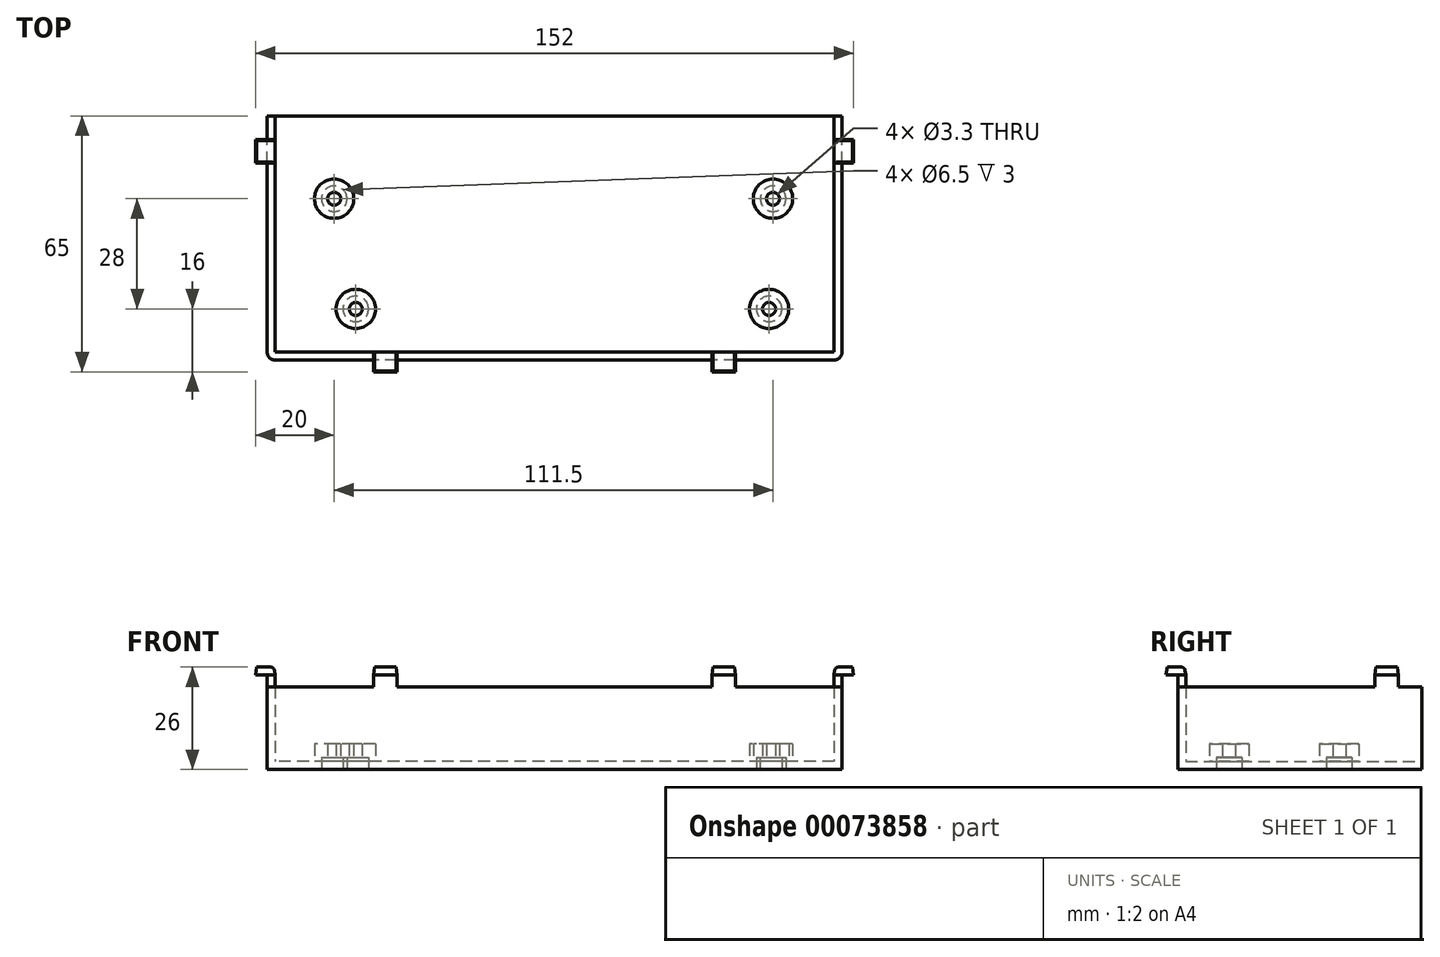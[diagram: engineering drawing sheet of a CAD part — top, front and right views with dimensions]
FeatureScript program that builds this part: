
annotation { "Feature Type Name" : "Feature", "Feature Type Description" : "" }
export const myFeature = defineFeature(function(context is Context, id is Id, definition is map)
    precondition{}
    {
        {
            var Q0;
            Q0=qCreatedBy(makeId("Top.planeOp"),FACE);
            var sketch = newSketch(context, id + "F0", { "sketchPlane" : qUnion([Q0])});
            skLineSegment(sketch, "E0.rect.bottom", {"start": v(71, -30) * mm, "end": v(-71, -30) * mm});
            skLineSegment(sketch, "E0.rect.top", {"start": v(71, 30) * mm, "end": v(-71, 30) * mm});
            skLineSegment(sketch, "E0.rect.left", {"start": v(71, -30) * mm, "end": v(71, 30) * mm});
            skLineSegment(sketch, "E0.rect.right", {"start": v(-71, -30) * mm, "end": v(-71, 30) * mm});
            skPoint(sketch, "E0.rect.middle", {"position": v(0, 0) * mm});
            skCircle(sketch, "E1", {"center": v(-56, 9) * mm, "radius": 5 * mm});
            skCircle(sketch, "E2", {"center": v(-50.5, -19) * mm, "radius": 5 * mm});
            skCircle(sketch, "E3", {"center": v(54.5, -19) * mm, "radius": 5 * mm});
            skCircle(sketch, "E4", {"center": v(55.5, 9) * mm, "radius": 5 * mm});
            skSolve(sketch);
        }
        {
            var Q0;
            Q0=makeQuery(id+"F0.imprint","IMPRINT",FACE,{"disambiguationData":[TD([[makeQuery(id+"F0.imprint","IMPRINT",EDGE,{"derivedFrom":sQuery(id+"F0.wireOp",EDGE,"E0.rect.bottom")}),-1.0]])]});
            var Q1;
            Q1=makeQuery(id+"F0.imprint","IMPRINT",FACE,{"disambiguationData":[TD([[makeQuery(id+"F0.imprint","IMPRINT",EDGE,{"derivedFrom":sQuery(id+"F0.wireOp",EDGE,"eba540f3-de09-4f47-9dca-2e5b0d6d8d7d")}),1.0]])]});
            var Q2;
            Q2=makeQuery(id+"F0.imprint","IMPRINT",FACE,{"disambiguationData":[TD([[makeQuery(id+"F0.imprint","IMPRINT",EDGE,{"derivedFrom":sQuery(id+"F0.wireOp",EDGE,"614f4d9e-865c-44ef-a343-09963b2743d6")}),1.0]])]});
            var Q3;
            Q3=makeQuery(id+"F0.imprint","IMPRINT",FACE,{"disambiguationData":[TD([[makeQuery(id+"F0.imprint","IMPRINT",EDGE,{"derivedFrom":sQuery(id+"F0.wireOp",EDGE,"847a5072-f3f1-48c5-a8f1-5cd9bb519ea2")}),1.0]])]});
            var Q4;
            Q4=makeQuery(id+"F0.imprint","IMPRINT",FACE,{"disambiguationData":[TD([[makeQuery(id+"F0.imprint","IMPRINT",EDGE,{"derivedFrom":sQuery(id+"F0.wireOp",EDGE,"b1afa658-efbe-457a-aa39-5f0282fc9bc2")}),-1.0]])]});
            var Q5;
            Q5=makeQuery(id+"F0.imprint","IMPRINT",FACE,{"disambiguationData":[TD([[makeQuery(id+"F0.imprint","IMPRINT",EDGE,{"derivedFrom":sQuery(id+"F0.wireOp",EDGE,"b1afa658-efbe-457a-aa39-5f0282fc9bc2")}),1.0]])]});
            var Q6;
            Q6=makeQuery(id+"F0.imprint","IMPRINT",FACE,{"disambiguationData":[TD([[makeQuery(id+"F0.imprint","IMPRINT",EDGE,{"derivedFrom":sQuery(id+"F0.wireOp",EDGE,"847a5072-f3f1-48c5-a8f1-5cd9bb519ea2")}),-1.0]])]});
            var Q7;
            Q7=makeQuery(id+"F0.imprint","IMPRINT",FACE,{"disambiguationData":[TD([[makeQuery(id+"F0.imprint","IMPRINT",EDGE,{"derivedFrom":sQuery(id+"F0.wireOp",EDGE,"eba540f3-de09-4f47-9dca-2e5b0d6d8d7d")}),-1.0]])]});
            var Q8;
            Q8=makeQuery(id+"F0.imprint","IMPRINT",FACE,{"disambiguationData":[TD([[makeQuery(id+"F0.imprint","IMPRINT",EDGE,{"derivedFrom":sQuery(id+"F0.wireOp",EDGE,"614f4d9e-865c-44ef-a343-09963b2743d6")}),-1.0]])]});
            var Q9;
            Q9=makeQuery(id+"F0.imprint","IMPRINT",FACE,{"disambiguationData":[TD([[makeQuery(id+"F0.imprint","IMPRINT",EDGE,{"derivedFrom":sQuery(id+"F0.wireOp",EDGE,"E1")}),1.0]])]});
            var Q10;
            Q10=makeQuery(id+"F0.imprint","IMPRINT",FACE,{"disambiguationData":[TD([[makeQuery(id+"F0.imprint","IMPRINT",EDGE,{"derivedFrom":sQuery(id+"F0.wireOp",EDGE,"E2")}),1.0]])]});
            var Q11;
            Q11=makeQuery(id+"F0.imprint","IMPRINT",FACE,{"disambiguationData":[TD([[makeQuery(id+"F0.imprint","IMPRINT",EDGE,{"derivedFrom":sQuery(id+"F0.wireOp",EDGE,"E3")}),1.0]])]});
            var Q12;
            Q12=makeQuery(id+"F0.imprint","IMPRINT",FACE,{"disambiguationData":[TD([[makeQuery(id+"F0.imprint","IMPRINT",EDGE,{"derivedFrom":sQuery(id+"F0.wireOp",EDGE,"E4")}),1.0]])]});
            extrude(context, id + "F1", {"entities" : qUnion([Q0, Q1, Q2, Q3, Q4, Q5, Q6, Q7, Q8, Q9, Q10, Q11, Q12]), "depth" : 19 * mm});
        }
        {
            var Q0;
            Q0=makeQuery(id+"F1.opExtrude","CAP_FACE",FACE,{"disambiguationData":[OSD([sQuery(id+"F0.wireOp",EDGE,"E0.rect.bottom"),sQuery(id+"F0.wireOp",EDGE,"E0.rect.top"),sQuery(id+"F0.wireOp",EDGE,"E0.rect.left"),sQuery(id+"F0.wireOp",EDGE,"E0.rect.right")])],"isStart":false});
            var Q1;
            Q1=makeQuery(id+"F1.opExtrude","SWEPT_FACE",FACE,{"disambiguationData":[OSD([sQuery(id+"F0.wireOp",EDGE,"E0.rect.top")])]});
            shell(context, id + "F2", {"entities" : qUnion([Q0, Q1]), "thickness" : 2 * mm, "oppositeDirection" : true});
        }
        {
            var Q0;
            Q0=makeQuery(id+"F1.opExtrude","SWEPT_EDGE",EDGE,{"disambiguationData":[OSD([sQuery(id+"F0.wireOp",EDGE,"E0.rect.bottom"),sQuery(id+"F0.wireOp",EDGE,"E0.rect.left")])]});
            var Q1;
            Q1=makeQuery(id+"F1.opExtrude","SWEPT_EDGE",EDGE,{"disambiguationData":[OSD([sQuery(id+"F0.wireOp",EDGE,"E0.rect.bottom"),sQuery(id+"F0.wireOp",EDGE,"E0.rect.right")])]});
            fillet(context, id + "F3", {"entities" : qUnion([Q0, Q1]), "radius" : 2 * mm, "tangentPropagation" : true, "allowEdgeOverflow" : false});
        }
        {
            var Q0;
            Q0=makeQuery(id+"F1.opExtrude","CAP_FACE",FACE,{"disambiguationData":[OSD([sQuery(id+"F0.wireOp",EDGE,"E0.rect.bottom"),sQuery(id+"F0.wireOp",EDGE,"E0.rect.top"),sQuery(id+"F0.wireOp",EDGE,"E0.rect.left"),sQuery(id+"F0.wireOp",EDGE,"E0.rect.right")])],"isStart":false});
            var sketch = newSketch(context, id + "F4", { "sketchPlane" : qUnion([Q0])});
            skLineSegment(sketch, "E5", {"start": v(0, 40.57) * mm, "end": v(0, -37.04) * mm, "construction": true});
            skLineSegment(sketch, "E6", {"start": v(-83.98, 0) * mm, "end": v(87.53, 0) * mm, "construction": true});
            skLineSegment(sketch, "E7.bottom", {"start": v(-46, -30) * mm, "end": v(-40, -30) * mm});
            skLineSegment(sketch, "E7.top", {"start": v(-46, -32) * mm, "end": v(-40, -32) * mm});
            skLineSegment(sketch, "E7.left", {"start": v(-46, -30) * mm, "end": v(-46, -32) * mm});
            skLineSegment(sketch, "E7.right", {"start": v(-40, -30) * mm, "end": v(-40, -32) * mm});
            skLineSegment(sketch, "E8.bottom", {"start": v(-73, 24) * mm, "end": v(-71, 24) * mm});
            skLineSegment(sketch, "E8.top", {"start": v(-73, 18) * mm, "end": v(-71, 18) * mm});
            skLineSegment(sketch, "E8.left", {"start": v(-73, 24) * mm, "end": v(-73, 18) * mm});
            skLineSegment(sketch, "E8.right", {"start": v(-71, 24) * mm, "end": v(-71, 18) * mm});
            skLineSegment(sketch, "E9.MirrorCS", {"start": v(73, 24) * mm, "end": v(71, 24) * mm});
            skLineSegment(sketch, "E10.MirrorCS", {"start": v(73, 24) * mm, "end": v(73, 18) * mm});
            skLineSegment(sketch, "E11.MirrorCS", {"start": v(71, 24) * mm, "end": v(71, 18) * mm});
            skLineSegment(sketch, "E12.MirrorCS", {"start": v(73, 18) * mm, "end": v(71, 18) * mm});
            skLineSegment(sketch, "E13.MirrorCS", {"start": v(46, -30) * mm, "end": v(40, -30) * mm});
            skLineSegment(sketch, "E14.MirrorCS", {"start": v(46, -30) * mm, "end": v(46, -32) * mm});
            skLineSegment(sketch, "E15.MirrorCS", {"start": v(40, -30) * mm, "end": v(40, -32) * mm});
            skLineSegment(sketch, "E16.MirrorCS", {"start": v(46, -32) * mm, "end": v(40, -32) * mm});
            skSolve(sketch);
        }
        {
            var Q0;
            Q0 = qSketchRegion(id + "F4", true);
            extrude(context, id + "F5", {"entities" : qUnion([Q0]), "operationType" : NewBodyOperationType.ADD, "depth" : 3 * mm});
        }
        {
            var Q0;
            Q0=makeQuery(id+"F5.opExtrude","CAP_FACE",FACE,{"disambiguationData":[OSD([sQuery(id+"F4.wireOp",EDGE,"E8.bottom"),sQuery(id+"F4.wireOp",EDGE,"E8.top"),sQuery(id+"F4.wireOp",EDGE,"E8.left"),sQuery(id+"F4.wireOp",EDGE,"E8.right")])],"isStart":false});
            var sketch = newSketch(context, id + "F6", { "sketchPlane" : qUnion([Q0])});
            skLineSegment(sketch, "E17.bottom", {"start": v(-71, 24) * mm, "end": v(-76, 24) * mm});
            skLineSegment(sketch, "E17.top", {"start": v(-71, 18) * mm, "end": v(-76, 18) * mm});
            skLineSegment(sketch, "E17.left", {"start": v(-71, 24) * mm, "end": v(-71, 18) * mm});
            skLineSegment(sketch, "E17.right", {"start": v(-76, 24) * mm, "end": v(-76, 18) * mm});
            skPoint(sketch, "E18.0", {"position": v(-46, -30) * mm});
            skPoint(sketch, "E18.1", {"position": v(-40, -30) * mm});
            skLineSegment(sketch, "E19.bottom", {"start": v(-46, -30) * mm, "end": v(-40, -30) * mm});
            skLineSegment(sketch, "E19.top", {"start": v(-46, -35) * mm, "end": v(-40, -35) * mm});
            skLineSegment(sketch, "E19.left", {"start": v(-46, -30) * mm, "end": v(-46, -35) * mm});
            skLineSegment(sketch, "E19.right", {"start": v(-40, -30) * mm, "end": v(-40, -35) * mm});
            skPoint(sketch, "E20.0", {"position": v(40, -30) * mm});
            skPoint(sketch, "E20.1", {"position": v(46, -30) * mm});
            skPoint(sketch, "E20.2", {"position": v(71, 18) * mm});
            skPoint(sketch, "E20.3", {"position": v(71, 24) * mm});
            skLineSegment(sketch, "E21.bottom", {"start": v(40, -30) * mm, "end": v(46, -30) * mm});
            skLineSegment(sketch, "E21.top", {"start": v(40, -35) * mm, "end": v(46, -35) * mm});
            skLineSegment(sketch, "E21.left", {"start": v(40, -30) * mm, "end": v(40, -35) * mm});
            skLineSegment(sketch, "E21.right", {"start": v(46, -30) * mm, "end": v(46, -35) * mm});
            skLineSegment(sketch, "E22.bottom", {"start": v(71, 18) * mm, "end": v(76, 18) * mm});
            skLineSegment(sketch, "E22.top", {"start": v(71, 24) * mm, "end": v(76, 24) * mm});
            skLineSegment(sketch, "E22.left", {"start": v(71, 18) * mm, "end": v(71, 24) * mm});
            skLineSegment(sketch, "E22.right", {"start": v(76, 18) * mm, "end": v(76, 24) * mm});
            skSolve(sketch);
        }
        {
            var Q0;
            Q0 = qSketchRegion(id + "F6", true);
            extrude(context, id + "F7", {"entities" : qUnion([Q0]), "operationType" : NewBodyOperationType.ADD, "depth" : 2 * mm, "hasDraft" : true, "draftAngle" : 8 * degree, "draftPullDirection" : true});
        }
        {
            var Q0;
            Q0=makeQuery(id+"F7.opExtrude","CAP_EDGE",EDGE,{"disambiguationData":[OSD([sQuery(id+"F6.wireOp",EDGE,"E17.left")])],"isStart":false});
            var Q1;
            Q1=makeQuery(id+"F7.opExtrude","CAP_EDGE",EDGE,{"disambiguationData":[OSD([sQuery(id+"F6.wireOp",EDGE,"E19.bottom")])],"isStart":false});
            var Q2;
            Q2=makeQuery(id+"F7.opExtrude","CAP_EDGE",EDGE,{"disambiguationData":[OSD([sQuery(id+"F6.wireOp",EDGE,"E21.bottom")])],"isStart":false});
            var Q3;
            Q3=makeQuery(id+"F7.opExtrude","CAP_EDGE",EDGE,{"disambiguationData":[OSD([sQuery(id+"F6.wireOp",EDGE,"E22.left")])],"isStart":false});
            fillet(context, id + "F8", {"entities" : qUnion([Q0, Q1, Q2, Q3]), "radius" : 1 * mm, "tangentPropagation" : true, "allowEdgeOverflow" : false});
        }
        {
            var Q0;
            Q0=makeQuery(id+"F0.imprint","IMPRINT",FACE,{"disambiguationData":[TD([[makeQuery(id+"F0.imprint","IMPRINT",EDGE,{"derivedFrom":sQuery(id+"F0.wireOp",EDGE,"E1")}),1.0]])]});
            var Q1;
            Q1=makeQuery(id+"F0.imprint","IMPRINT",FACE,{"disambiguationData":[TD([[makeQuery(id+"F0.imprint","IMPRINT",EDGE,{"derivedFrom":sQuery(id+"F0.wireOp",EDGE,"E4")}),1.0]])]});
            var Q2;
            Q2=makeQuery(id+"F0.imprint","IMPRINT",FACE,{"disambiguationData":[TD([[makeQuery(id+"F0.imprint","IMPRINT",EDGE,{"derivedFrom":sQuery(id+"F0.wireOp",EDGE,"E3")}),1.0]])]});
            var Q3;
            Q3=makeQuery(id+"F0.imprint","IMPRINT",FACE,{"disambiguationData":[TD([[makeQuery(id+"F0.imprint","IMPRINT",EDGE,{"derivedFrom":sQuery(id+"F0.wireOp",EDGE,"E2")}),1.0]])]});
            extrude(context, id + "F9", {"entities" : qUnion([Q0, Q1, Q2, Q3]), "operationType" : NewBodyOperationType.ADD, "depth" : 4.5 * mm});
        }
        {
            var Q0;
            Q0=makeQuery(id+"F1.opExtrude","CAP_FACE",FACE,{"disambiguationData":[OSD([sQuery(id+"F0.wireOp",EDGE,"E0.rect.bottom"),sQuery(id+"F0.wireOp",EDGE,"E0.rect.top"),sQuery(id+"F0.wireOp",EDGE,"E0.rect.left"),sQuery(id+"F0.wireOp",EDGE,"E0.rect.right")])],"isStart":true});
            var sketch = newSketch(context, id + "F10", { "sketchPlane" : qUnion([Q0])});
            skPoint(sketch, "E23.0", {"position": v(-50.5, 19) * mm});
            skPoint(sketch, "E23.1", {"position": v(-56, -9) * mm});
            skPoint(sketch, "E23.2", {"position": v(55.5, -9) * mm});
            skPoint(sketch, "E23.3", {"position": v(54.5, 19) * mm});
            skSolve(sketch);
        }
        {
            var Q0;
            Q0=sQuery(id+"F10.wireOp",VERTEX,"E23.0");
            var Q1;
            Q1=sQuery(id+"F10.wireOp",VERTEX,"E23.1");
            var Q2;
            Q2=sQuery(id+"F10.wireOp",VERTEX,"E23.2");
            var Q3;
            Q3=sQuery(id+"F10.wireOp",VERTEX,"E23.3");
            var Q4;
            Q4=makeQuery(id+"F1.opExtrude","SWEPT_BODY",BODY,{"disambiguationData":[OSD([sQuery(id+"F0.wireOp",EDGE,"E0.rect.bottom"),sQuery(id+"F0.wireOp",EDGE,"E0.rect.top"),sQuery(id+"F0.wireOp",EDGE,"E0.rect.left"),sQuery(id+"F0.wireOp",EDGE,"E0.rect.right")])]});
            hole(context, id + "F11", {"style" : HoleStyle.C_BORE, "holeDiameter" : 3.3 * mm, "cBoreDiameter" : 6.5 * mm, "cBoreDepth" : 3 * mm, "endStyle" : HoleEndStyle.THROUGH, "locations" : qUnion([Q0, Q1, Q2, Q3]), "scope" : qUnion([Q4]), "standardTappedOrClearance" : lookupTablePath({ "standard" : "ISO", "fit" : "Normal", "size" : "M3", "type" : "Clearance" }), "standardBlindInLast" : lookupTablePath({ "fit" : "Standard", "standard" : "ISO", "size" : "M3", "type" : "Clearance" }), "isTappedThrough" : true});
        }
    });
